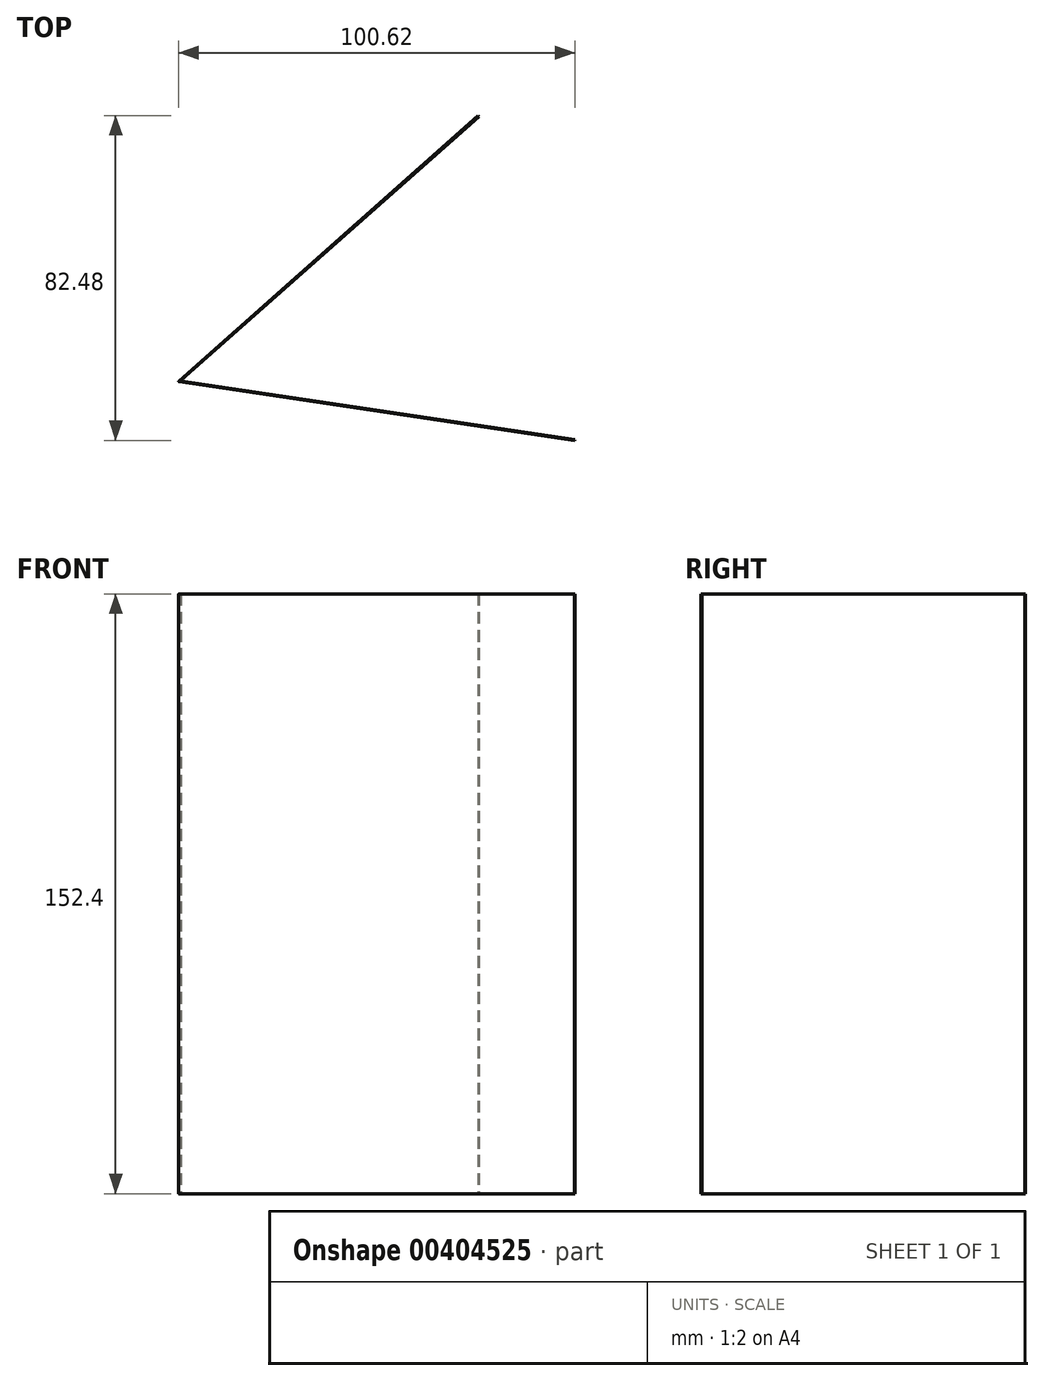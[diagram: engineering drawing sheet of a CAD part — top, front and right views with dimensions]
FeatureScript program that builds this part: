
annotation { "Feature Type Name" : "Feature", "Feature Type Description" : "" }
export const myFeature = defineFeature(function(context is Context, id is Id, definition is map)
    precondition{}
    {
        {
            var Q0;
            Q0=qCreatedBy(makeId("Top.planeOp"),FACE);
            var sketch = newSketch(context, id + "F0", { "sketchPlane" : qUnion([Q0])});
            skLineSegment(sketch, "E0", {"start": v(-3.25, 100.55) * mm, "end": v(-79.27, 33.15) * mm});
            skLineSegment(sketch, "E1", {"start": v(-79.22, 32.98) * mm, "end": v(21.28, 18.07) * mm});
            skLineSegment(sketch, "E2", {"start": v(21.28, 18.07) * mm, "end": v(21.32, 18.31) * mm});
            skLineSegment(sketch, "E3", {"start": v(21.32, 18.31) * mm, "end": v(-78.65, 33.15) * mm});
            skLineSegment(sketch, "E4", {"start": v(-78.7, 33.32) * mm, "end": v(-3.08, 100.37) * mm});
            skLineSegment(sketch, "E5", {"start": v(-3.08, 100.37) * mm, "end": v(-3.25, 100.55) * mm});
            skPoint(sketch, "E6.visualSharp", {"position": v(-79.43, 33) * mm});
            skArc(sketch, "E6.filletArc", {"start": v(-79.27, 33.15) * mm, "mid": v(-79.3, 33.05) * mm, "end": v(-79.22, 32.98) * mm});
            skPoint(sketch, "E7.visualSharp", {"position": v(-78.86, 33.18) * mm});
            skArc(sketch, "E7.filletArc", {"start": v(-78.7, 33.32) * mm, "mid": v(-78.73, 33.22) * mm, "end": v(-78.65, 33.15) * mm});
            skSolve(sketch);
        }
        {
            var Q0;
            Q0 = qSketchRegion(id + "F0", true);
            extrude(context, id + "F1", {"entities" : qUnion([Q0]), "depth" : 152.4 * mm});
        }
    });
